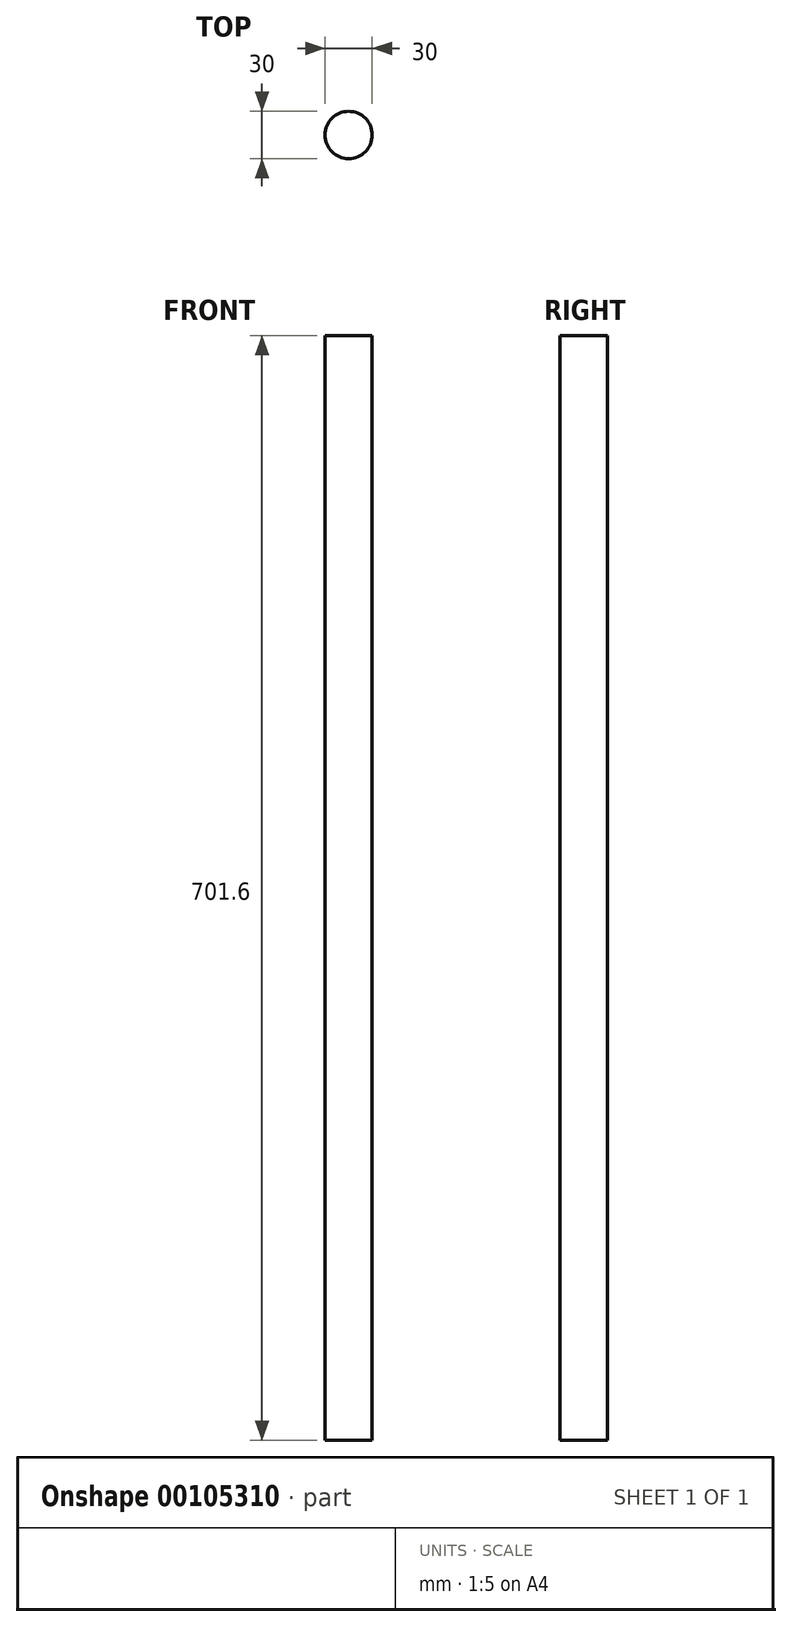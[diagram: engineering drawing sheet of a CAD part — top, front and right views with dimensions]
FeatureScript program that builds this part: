
annotation { "Feature Type Name" : "Feature", "Feature Type Description" : "" }
export const myFeature = defineFeature(function(context is Context, id is Id, definition is map)
    precondition{}
    {
        {
            var Q0;
            Q0=qCreatedBy(makeId("Top.planeOp"),FACE);
            var sketch = newSketch(context, id + "F0", { "sketchPlane" : qUnion([Q0])});
            skCircle(sketch, "E0", {"center": v(0, 0) * mm, "radius": 15 * mm});
            skSolve(sketch);
        }
        {
            var Q0;
            Q0 = qSketchRegion(id + "F0", true);
            var Q1;
            Q1=makeQuery(id+"F0.imprint","IMPRINT",FACE,{"disambiguationData":[TD([[makeQuery(id+"F0.imprint","IMPRINT",EDGE,{"derivedFrom":sQuery(id+"F0.wireOp",EDGE,"E0")}),1.0]])]});
            extrude(context, id + "F1", {"entities" : qUnion([Q0, Q1]), "depth" : 25.4 * mm});
        }
        {
            var Q0;
            Q0=makeQuery(id+"F1.opExtrude","CAP_FACE",FACE,{"disambiguationData":[OSD([sQuery(id+"F0.wireOp",EDGE,"E0")])],"isStart":false});
            extrude(context, id + "F2", {"entities" : qUnion([Q0]), "operationType" : NewBodyOperationType.ADD, "depth" : 600 * mm});
        }
        {
            var Q0;
            Q0=makeQuery(id+"F2.opExtrude","CAP_FACE",FACE,{"disambiguationData":[OSD([sQuery(id+"F0.wireOp",EDGE,"E0")])],"isStart":false});
            extrude(context, id + "F3", {"entities" : qUnion([Q0]), "operationType" : NewBodyOperationType.ADD, "depth" : 25.4 * mm});
        }
        {
            var Q0;
            Q0=makeQuery(id+"F3.opExtrude","CAP_FACE",FACE,{"disambiguationData":[OSD([sQuery(id+"F0.wireOp",EDGE,"E0")])],"isStart":false});
            var Q1;
            Q1=makeQuery(id+"F1.opExtrude","CAP_FACE",FACE,{"disambiguationData":[OSD([sQuery(id+"F0.wireOp",EDGE,"E0")])],"isStart":true});
            extrude(context, id + "F4", {"entities" : qUnion([Q0, Q1]), "operationType" : NewBodyOperationType.ADD, "depth" : 25.4 * mm});
        }
        {
            var Q0;
            {var subQ0=sQuery(id+"F0.wireOp",EDGE,"E0");Q0=makeQuery(id+"F4.opExtrude","CAP_FACE",FACE,{"disambiguationData":[OSD([subQ0]),TDD([makeQuery(id+"F3.opExtrude","CAP_FACE",FACE,{"disambiguationData":[OSD([subQ0])],"isStart":false})])],"isStart":false});}
            extrude(context, id + "F5", {"entities" : qUnion([Q0]), "operationType" : NewBodyOperationType.ADD, "depth" : 25.4 * mm});
        }
    });
